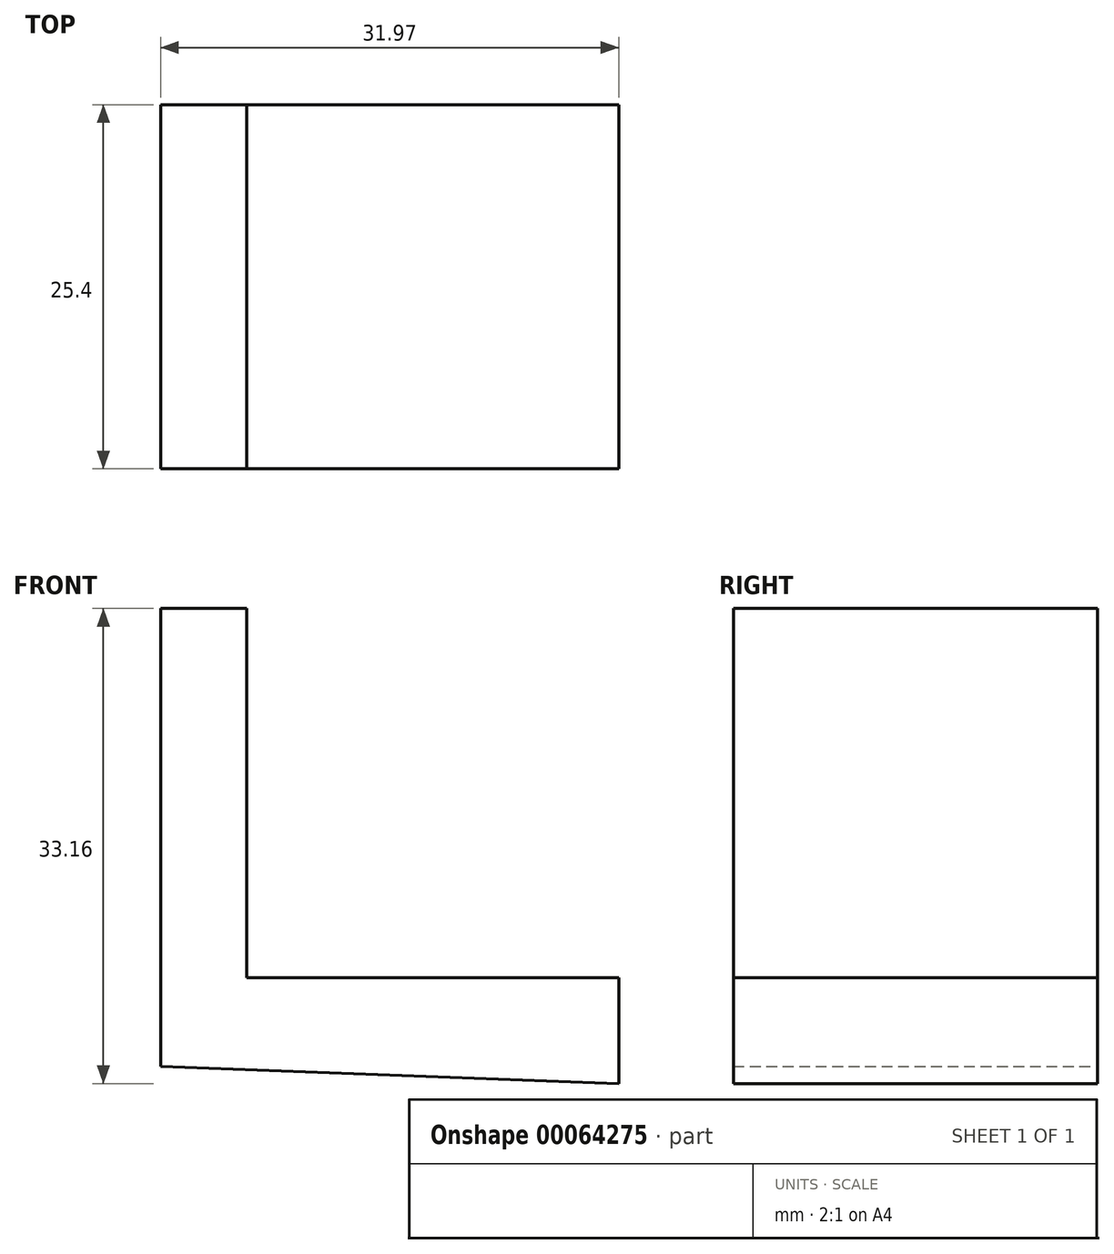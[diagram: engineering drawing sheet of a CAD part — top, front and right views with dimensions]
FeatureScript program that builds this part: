
annotation { "Feature Type Name" : "Feature", "Feature Type Description" : "" }
export const myFeature = defineFeature(function(context is Context, id is Id, definition is map)
    precondition{}
    {
        {
            var Q0;
            Q0=qCreatedBy(makeId("Front.planeOp"),FACE);
            var sketch = newSketch(context, id + "F0", { "sketchPlane" : qUnion([Q0])});
            skLineSegment(sketch, "E0", {"start": v(-47.85, 28.87) * mm, "end": v(-47.85, 60.83) * mm});
            skLineSegment(sketch, "E1", {"start": v(-47.85, 60.83) * mm, "end": v(-41.85, 60.83) * mm});
            skLineSegment(sketch, "E2", {"start": v(-41.85, 60.83) * mm, "end": v(-41.85, 35.06) * mm});
            skLineSegment(sketch, "E3", {"start": v(-41.85, 35.06) * mm, "end": v(-15.88, 35.06) * mm});
            skLineSegment(sketch, "E4", {"start": v(-15.88, 35.06) * mm, "end": v(-15.88, 27.67) * mm});
            skLineSegment(sketch, "E5", {"start": v(-15.88, 27.67) * mm, "end": v(-47.85, 28.87) * mm});
            skSolve(sketch);
        }
        {
            var Q0;
            Q0=makeQuery(id+"F0.imprint","IMPRINT",FACE,{"disambiguationData":[TD([[makeQuery(id+"F0.imprint","IMPRINT",EDGE,{"derivedFrom":sQuery(id+"F0.wireOp",EDGE,"E0")}),-1.0]])]});
            extrude(context, id + "F1", {"entities" : qUnion([Q0]), "depth" : 25.4 * mm});
        }
    });
